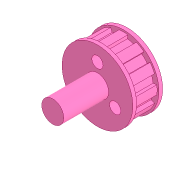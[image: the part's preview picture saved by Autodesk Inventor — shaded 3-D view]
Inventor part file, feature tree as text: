
AUTODESK INVENTOR PART (.ipt)
format: ipt  version: 2022.5 (Build 265521000, 521)  size: 189,952 bytes
history: native  units: in
note: dims shown in document units (in); Inventor stores cm internally (conversion verified against a paired STEP export)
features: sketch x4, extrude x3, pattern_circular x2, revolve x1
ambient origin geometry x8: Origin, YZ Plane, XZ Plane, XY Plane, X Axis, Y Axis, Z Axis, Center Point
bodies: Body1 (feature_tree)
feature tree (10):
  revolve  "Revolution4"  [1 undecoded]
  extrude  "Extrusion16"  Depth=0.0016in
  extrude  "Extrusion17"  Depth=0.2362in
  pattern_circular  "Circular Pattern1"  [2 undecoded]
  extrude  "Extrusion18"  Depth=0.1181in
  pattern_circular  "Circular Pattern2"  [2 undecoded]
  sketch  "Sketch19"  dims[d111=0.0394in d113=0.1181in]
  sketch  "Sketch20"  dims[d115=90.0deg d116=0.0016in]
  sketch  "Sketch21"  dims[d117=0.7874in d118=0.0in d119=0.2362in]
  sketch  "Sketch22"  dims[d120=0.0591in d121=0.315in d122=0.1181in d123=0.0in d124=0.0in d125=1.1811in d126=360.0deg d128=0.0394in d129=15.0deg d130=0.3937in d131=0.0in d132=4.7244in d133=360.0deg]
note: 5 required parameter values undecoded (feature->parameter linkage not recoverable at this tier; creation-order binding heuristic only, values carry confidence <= 0.55)